# Revit family: Plumbing_Fixtures_Grohe_Eurosmart_Cosmopolitan_E-Infra-red_Basin_Tap_36269000_14_METRIC
name_source: partatom
category: Plumbing Fixtures
revit_build: Autodesk Revit 2014 (Build: 20130308_1515(x64)
units: mm (PartAtom-declared; Revit-internal decimal feet)

## types (1)
- Plumbing_Fixtures_Grohe_Eurosmart_Cosmopolitan_E-Infra-red_Basin_Tap_36269000_14_METRIC
    ADA Compliant = Yes
    Assembly Code = C1030220
    AssetType = Fixed
    CW Connection = Yes
    CWFU = 4.5
    ClassificationName = Uniclass2015
    ClassificationValue = Pr_40_20_87_98
    Cold Water Connection Diameter = 10 mm  [stored 0.0328084 ft]
    Cold Water Radius = 5 mm  [stored 0.0164042 ft]
    Color = Chrome
    Cost = 0 $
    Default Elevation = 600 mm
    Description = Reflecting the core values of Minimalism, Eurosmart Cosmopolitan is the modern favorite in the bathroom. Finished in sparkling GROHE StarLight® chrome, the conical transition from the faucet body to the lever handle conveys a refined form without sacrificing solidity. An extensive line up of products brings architectural design preferences to a wider audience and includes four styles of basin faucet to complement the latest bathroom ceramics. For improved user comfort, the lozenge-shaped lever handle is pitched at an angle of seven degrees and benefits from GROHE SilkMove®  our superior cartridge technology, which delivers lifelong smooth handling across the collection.
    DocumentationCertificates = http://www.grohe.com
    DocumentationInstallationGuide = http://www.grohe.com
    DocumentationLiterature = http://cdn08.grohe.com
    DocumentationMaintenance = http://cdn08.grohe.com
    DocumentationTechnical = http://cdn08.grohe.com
    DurationUnit = Years
    Ecojoy = Yes
    ExpectedLife = 0
    Faucet Material = Grohe-Chrome
    Finish = Chrome
    Flow Pressure = min 0.05MPa/recommended 0.1 - 0.6MPa
    Flow Rate = approx 6 L/min
    HW Connection = Yes
    HWFU = 4.5
    Height = 125 mm  [stored 0.410105 ft]
    Hot Water Connection Diameter = 10 mm  [stored 0.0328084 ft]
    Hot Water Radius = 5 mm  [stored 0.0164042 ft]
    Keynote = N13
    Length = 48 mm  [stored 0.15748 ft]
    Low Emitting Material = Yes
    Manufacturer = Grohe AG
    Material = Chrome
    Mixing Leaver = Yes
    Model = Euroeco Cosmopolitan E 36269 000
    ModelNumber = 36269000
    NBSDescription = Water supply fittings for wash basins and troughs
    NBSObjectName = Washbasin taps
    NBSReference = 45-35-70/371
    Name = Euroeco Cosmopolitan E 36269 000
    Operating Pressure = max 1MPa
    Percentage of Recycled Content = 0
    Product Documentation Link = http://cdn08.grohe.com
    Product Page URL = http://www.grohe.com
    ProductionYear = 2015
    Spare Parts List = http://www.grohe.com
    Temp - Hot Water Supply = max 70 deg C
    Temp - Hot Water Supply (Recommended) = 60 deg C
    Type Comments = Infra-red electronic basin mixer, 6V litium battery, type CR-P2
    TypeName = Infra-red electronic basin mixer, 6V litium battery, type CR-P2
    URL = www.grohe.com
    Vent Connection = No
    WFU = 0
    WarrantyDurationUnit = Years
    Waste Connection = No
    Width = 145 mm  [stored 0.475722 ft]
    _BIMspec_GUID = 0
    _current revision = 2
    _distributed by = www.bimstore.co.uk

note: [stored X ft] marks values corroborated as IEEE doubles in the binary element streams (Revit-internal decimal feet)

## geometry (parser evidence)
native form markers: Blend x6, Sweep x1
no freeform markers — native parametric forms only
